# Revit family: Enclosure
name_source: partatom
category: Generic Models
units: mm (PartAtom-declared; Revit-internal decimal feet)

## family parameters
Always vertical = Yes
Can host rebar = No
Cut with Voids When Loaded = No
Maintain Annotation Orientation = No
Part Type = Normal
Room Calculation Point = No
Round Connector Dimension = Use Diameter
Shared = No
Work Plane-Based = No

## types (1)
- Enclosure
    Angle of Inclination = 30.00°
    Default Elevation = 0 mm  [stored 0 ft]
    Enclosure Half Width = 1000 mm  [stored 3.28084 ft]
    Enclosure Perimeter = 50 mm  [stored 0.164042 ft]
    Height of Enclosure = 750 mm  [stored 2.46063 ft]
    Lower Landing = 1500 mm  [stored 4.92126 ft]
    Lower Landing Horizontal = 1299 mm
    Perimeter Height = 750 mm  [stored 2.46063 ft]
    Rise = 3000 mm  [stored 9.84252 ft]
    Thickness of Enclosure = 100 mm  [stored 0.328084 ft]
    Transition Length = 5196 mm
    Upper Landing = 1500 mm  [stored 4.92126 ft]
    Upper Landing Horizontal = 1701 mm

note: [stored X ft] marks values corroborated as IEEE doubles in the binary element streams (Revit-internal decimal feet)

## geometry (parser evidence)
native form markers: Sweep x3
no freeform markers — native parametric forms only
